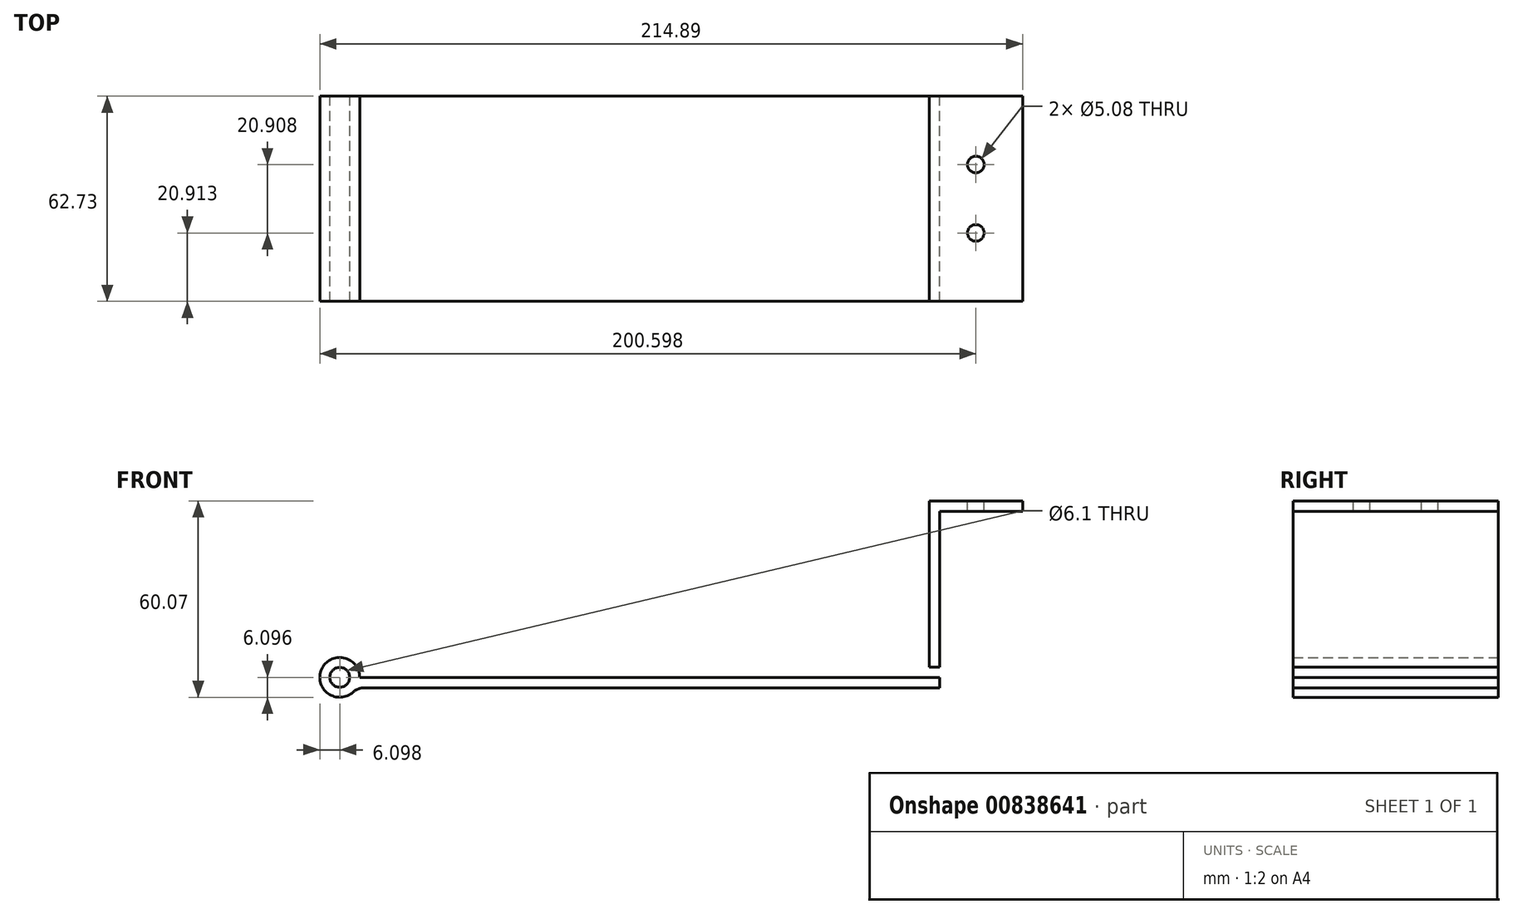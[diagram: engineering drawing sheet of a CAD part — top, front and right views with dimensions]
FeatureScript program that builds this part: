
annotation { "Feature Type Name" : "Feature", "Feature Type Description" : "" }
export const myFeature = defineFeature(function(context is Context, id is Id, definition is map)
    precondition{}
    {
        {
            var Q0;
            Q0=qCreatedBy(makeId("Front.planeOp"),FACE);
            var sketch = newSketch(context, id + "F0", { "sketchPlane" : qUnion([Q0])});
            skCircle(sketch, "E0", {"center": v(-53.3, 14.44) * mm, "radius": 6.1 * mm});
            skCircle(sketch, "E1", {"center": v(-53.3, 14.44) * mm, "radius": 3.05 * mm});
            skLineSegment(sketch, "E2.bottom", {"start": v(-47.2, 17.61) * mm, "end": v(130.09, 17.61) * mm});
            skLineSegment(sketch, "E2.top", {"start": v(-47.2, 11.26) * mm, "end": v(130.09, 11.26) * mm});
            skLineSegment(sketch, "E2.left", {"start": v(-47.2, 17.61) * mm, "end": v(-47.2, 11.26) * mm});
            skLineSegment(sketch, "E2.right", {"start": v(130.09, 17.61) * mm, "end": v(130.09, 11.26) * mm});
            skPoint(sketch, "E3", {"position": v(-47.2, 14.44) * mm});
            skLineSegment(sketch, "E4", {"start": v(-47.2, 17.61) * mm, "end": v(-48.1, 17.61) * mm});
            skLineSegment(sketch, "E5", {"start": v(-47.2, 11.26) * mm, "end": v(-48.1, 11.26) * mm});
            skLineSegment(sketch, "E6", {"start": v(-53.3, 14.44) * mm, "end": v(-53.3, 11.39) * mm});
            skLineSegment(sketch, "E7", {"start": v(-53.3, 11.39) * mm, "end": v(-53.3, 17.48) * mm});
            skLineSegment(sketch, "E8.MirrorCS", {"start": v(-59.4, 17.61) * mm, "end": v(-58.5, 17.61) * mm});
            skLineSegment(sketch, "E9.MirrorCS", {"start": v(-59.4, 11.26) * mm, "end": v(-58.5, 11.26) * mm});
            skLineSegment(sketch, "E10.MirrorCS", {"start": v(-59.4, 11.26) * mm, "end": v(-236.7, 11.26) * mm});
            skLineSegment(sketch, "E11.MirrorCS", {"start": v(-59.4, 17.61) * mm, "end": v(-236.7, 17.61) * mm});
            skLineSegment(sketch, "E12.MirrorCS", {"start": v(-236.7, 17.61) * mm, "end": v(-236.7, 11.26) * mm});
            skLineSegment(sketch, "E13", {"start": v(-47.2, 14.44) * mm, "end": v(130.09, 14.44) * mm});
            skLineSegment(sketch, "E14.bottom", {"start": v(130.09, 14.44) * mm, "end": v(126.91, 14.44) * mm});
            skLineSegment(sketch, "E14.top", {"start": v(130.09, 68.41) * mm, "end": v(126.91, 68.41) * mm});
            skLineSegment(sketch, "E14.left", {"start": v(130.09, 14.44) * mm, "end": v(130.09, 68.41) * mm});
            skLineSegment(sketch, "E14.right", {"start": v(126.91, 14.44) * mm, "end": v(126.91, 68.41) * mm});
            skLineSegment(sketch, "E15.bottom", {"start": v(130.09, 68.41) * mm, "end": v(155.49, 68.41) * mm});
            skLineSegment(sketch, "E15.top", {"start": v(130.09, 65.24) * mm, "end": v(155.49, 65.24) * mm});
            skLineSegment(sketch, "E15.left", {"start": v(130.09, 68.41) * mm, "end": v(130.09, 65.24) * mm});
            skLineSegment(sketch, "E15.right", {"start": v(155.49, 68.41) * mm, "end": v(155.49, 65.24) * mm});
            skSolve(sketch);
        }
        {
            var Q0;
            {var subQ0=sQuery(id+"F0.wireOp",EDGE,"E5");Q0=makeQuery(id+"F0.imprint","IMPRINT",FACE,{"disambiguationData":[TD([[makeQuery(id+"F0.imprint","IMPRINT",EDGE,{"derivedFrom":subQ0}),-1.0]])]});}
            var Q1;
            {var subQ0=sQuery(id+"F0.wireOp",EDGE,"E2.top");Q1=makeQuery(id+"F0.imprint","IMPRINT",FACE,{"disambiguationData":[TD([[makeQuery(id+"F0.imprint","IMPRINT",EDGE,{"derivedFrom":subQ0}),1.0]])]});}
            var Q2;
            {var subQ0=sQuery(id+"F0.wireOp",EDGE,"E0");var subQ4=makeQuery(id+"F0.imprint","INTERSECT",VERTEX,{"derivedFrom":[subQ0,sQuery(id+"F0.wireOp",EDGE,"E4")]});Q2=makeQuery(id+"F0.imprint","IMPRINT",FACE,{"disambiguationData":[TD([[makeQuery(id+"F0.imprint","IMPRINT",EDGE,{"disambiguationData":[TD([[subQ4,-1.0]])],"derivedFrom":subQ0}),1.0]])]});}
            var Q3;
            {var subQ5=sQuery(id+"F0.wireOp",EDGE,"E14.top");Q3=makeQuery(id+"F0.imprint","IMPRINT",FACE,{"disambiguationData":[TD([[makeQuery(id+"F0.imprint","IMPRINT",EDGE,{"derivedFrom":subQ5}),1.0]])]});}
            var Q4;
            {var subQ5=sQuery(id+"F0.wireOp",EDGE,"E14.bottom");Q4=makeQuery(id+"F0.imprint","IMPRINT",FACE,{"disambiguationData":[TD([[makeQuery(id+"F0.imprint","IMPRINT",EDGE,{"derivedFrom":subQ5}),-1.0]])]});}
            var Q5;
            Q5=makeQuery(id+"F0.imprint","IMPRINT",FACE,{"disambiguationData":[TD([[makeQuery(id+"F0.imprint","IMPRINT",EDGE,{"derivedFrom":sQuery(id+"F0.wireOp",EDGE,"E15.bottom")}),-1.0]])]});
            extrude(context, id + "F1", {"entities" : qUnion([Q0, Q1, Q2, Q3, Q4, Q5]), "depth" : 62.73 * mm, "offsetDistance" : 25.4 * mm});
        }
        {
            var Q0;
            Q0=makeQuery(id+"F1.opExtrude","SWEPT_EDGE",EDGE,{"disambiguationData":[OSD([sQuery(id+"F0.wireOp",EDGE,"E0"),sQuery(id+"F0.wireOp",EDGE,"E4")])]});
            var Q1;
            Q1=makeQuery(id+"F1.opExtrude","SWEPT_EDGE",EDGE,{"disambiguationData":[OSD([sQuery(id+"F0.wireOp",EDGE,"E0"),sQuery(id+"F0.wireOp",EDGE,"E5")])]});
            fillet(context, id + "F2", {"entities" : qUnion([Q0, Q1]), "radius" : 5.08 * mm, "tangentPropagation" : true, "allowEdgeOverflow" : false});
        }
        {
            var Q0;
            Q0=makeQuery(id+"F1.opExtrude","SWEPT_FACE",FACE,{"disambiguationData":[OSD([sQuery(id+"F0.wireOp",EDGE,"E14.top"),sQuery(id+"F0.wireOp",EDGE,"E15.bottom")])]});
            var sketch = newSketch(context, id + "F3", { "sketchPlane" : qUnion([Q0])});
            skPoint(sketch, "E16", {"position": v(141.2, -41.82) * mm});
            skPoint(sketch, "E16.positionSnap0", {"position": v(141.2, -62.73) * mm});
            skPoint(sketch, "E17", {"position": v(141.2, -20.9) * mm});
            skPoint(sketch, "E17.positionSnap0", {"position": v(141.2, 0) * mm});
            skCircle(sketch, "E18", {"center": v(141.2, -20.9) * mm, "radius": 2.54 * mm});
            skCircle(sketch, "E19", {"center": v(141.2, -41.82) * mm, "radius": 2.54 * mm});
            skSolve(sketch);
        }
        {
            var Q0;
            Q0 = qSketchRegion(id + "F3", true);
            extrude(context, id + "F4", {"entities" : qUnion([Q0]), "operationType" : NewBodyOperationType.REMOVE, "endBound" : BoundingType.THROUGH_ALL, "oppositeDirection" : true, "depth" : 25.4 * mm, "offsetDistance" : 25.4 * mm});
        }
    });
